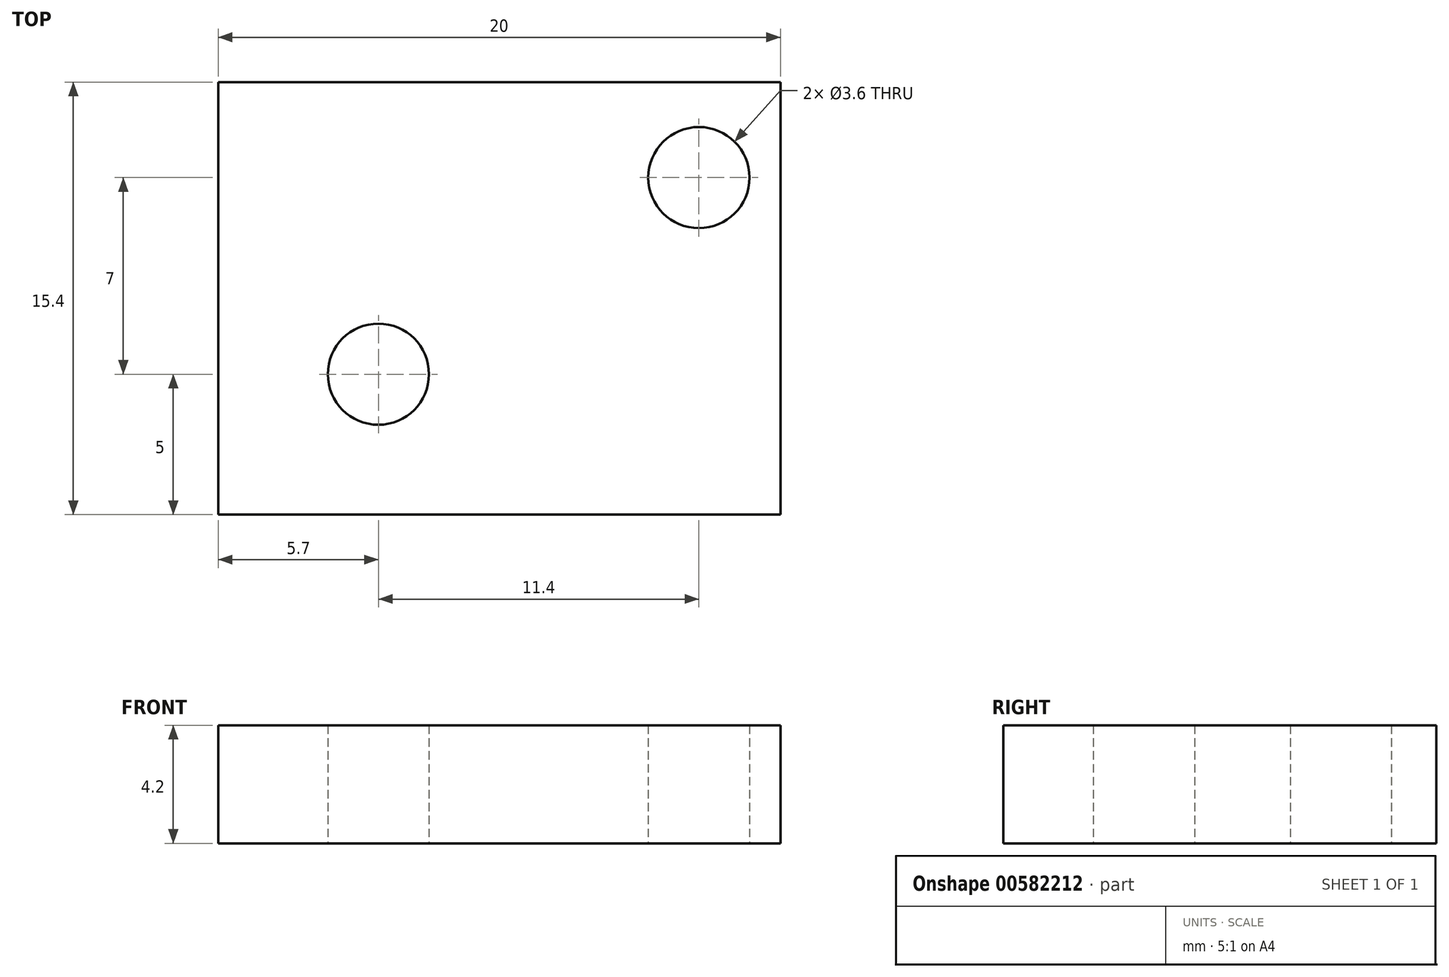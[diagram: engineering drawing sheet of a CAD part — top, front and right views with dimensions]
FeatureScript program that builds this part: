
annotation { "Feature Type Name" : "Feature", "Feature Type Description" : "" }
export const myFeature = defineFeature(function(context is Context, id is Id, definition is map)
    precondition{}
    {
        {
            var Q0;
            Q0=qCreatedBy(makeId("Top.planeOp"),FACE);
            var sketch = newSketch(context, id + "F0", { "sketchPlane" : qUnion([Q0])});
            skLineSegment(sketch, "E0.bottom", {"start": v(-10, 7.7) * mm, "end": v(10, 7.7) * mm});
            skLineSegment(sketch, "E0.top", {"start": v(-10, -7.7) * mm, "end": v(10, -7.7) * mm});
            skLineSegment(sketch, "E0.left", {"start": v(-10, 7.7) * mm, "end": v(-10, -7.7) * mm});
            skLineSegment(sketch, "E0.right", {"start": v(10, 7.7) * mm, "end": v(10, -7.7) * mm});
            skPoint(sketch, "E0.middle", {"position": v(0, 0) * mm});
            skCircle(sketch, "E1", {"center": v(7.1, 4.3) * mm, "radius": 1.8 * mm});
            skCircle(sketch, "E2", {"center": v(-4.3, -2.7) * mm, "radius": 1.8 * mm});
            skSolve(sketch);
        }
        {
            var Q0;
            Q0=makeQuery(id+"F0.imprint","IMPRINT",FACE,{"disambiguationData":[TD([[makeQuery(id+"F0.imprint","IMPRINT",EDGE,{"derivedFrom":sQuery(id+"F0.wireOp",EDGE,"E0.bottom")}),-1.0]])]});
            extrude(context, id + "F1", {"entities" : qUnion([Q0]), "depth" : 4.2 * mm, "offsetDistance" : 25 * mm});
        }
    });
